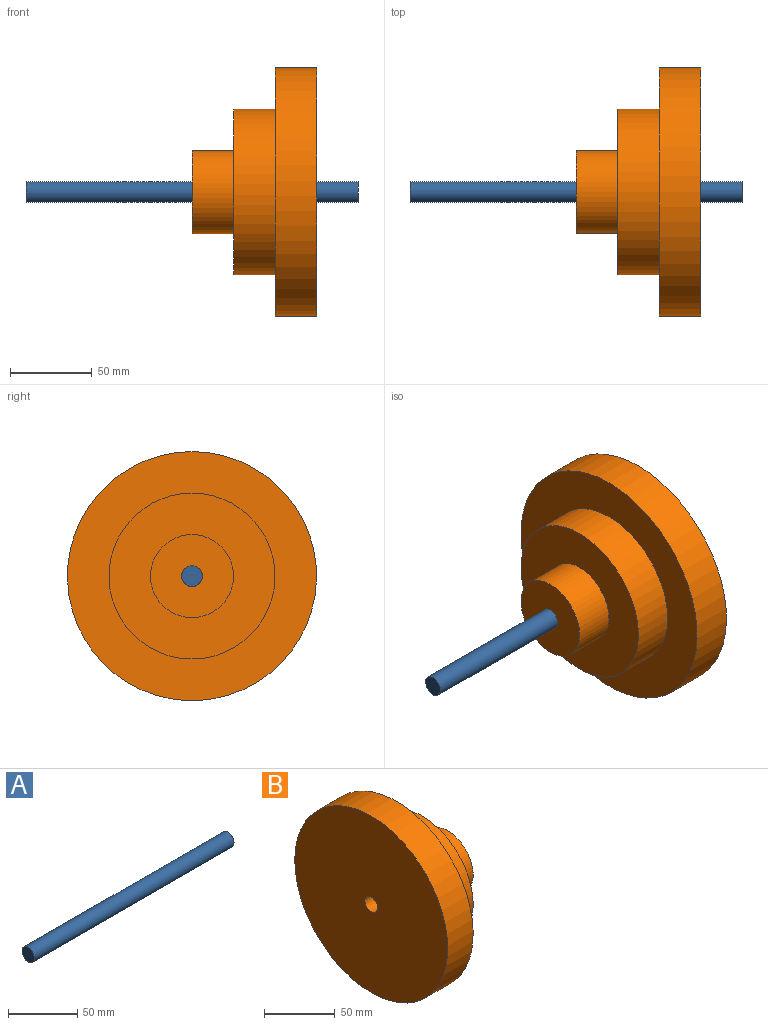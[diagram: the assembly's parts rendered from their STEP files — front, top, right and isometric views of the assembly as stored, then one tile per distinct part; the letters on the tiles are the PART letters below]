
ASSEMBLY  parts=2 mates=1
PART A: 3 faces, bbox 203.2x12.7x12.7 mm
  f0: cylinder r=6.35mm len=203.2mm, axis (-1,0,0), area 8107.3mm2, adj f1,f2
  f1: plane 12.7x12.7mm, normal (1,0,0), area 126.7mm2, adj f0
  f2: plane 12.7x12.7mm, normal (-1,0,0), area 126.7mm2, adj f0
PART B: 8 faces, bbox 76.2x152.4x152.4 mm
  f0: cylinder r=76.2mm len=152.4mm, axis (-1,0,0), area 12161mm2, adj f1,f2
  f1: plane 152.4x152.4mm, normal (1,0,0), area 10134.1mm2, adj f0,f3
  f2: plane 152.4x152.4mm, normal (-1,0,0), area 18114.8mm2, adj f0,f7
  f3: cylinder r=50.8mm len=101.6mm, axis (-1,0,0), area 8107.3mm2, adj f1,f4
  f4: plane 101.6x101.6mm, normal (1,0,0), area 6080.5mm2, adj f3,f5
  f5: cylinder r=25.4mm len=50.8mm, axis (-1,0,0), area 4053.7mm2, adj f4,f6
  f6: plane 50.8x50.8mm, normal (1,0,0), area 1900.2mm2, adj f5,f7
  f7: cylinder r=6.35mm len=76.2mm, axis (1,0,0), area 3040.2mm2, adj f2,f6
PLACE A at identity
PLACE B rot(axis=(0,1,0),180deg) t=(177.8,0,0)mm
MATE fastened B.f5 <-> A.f0  axis (1,0,0) through (101.6,0,0)mm
